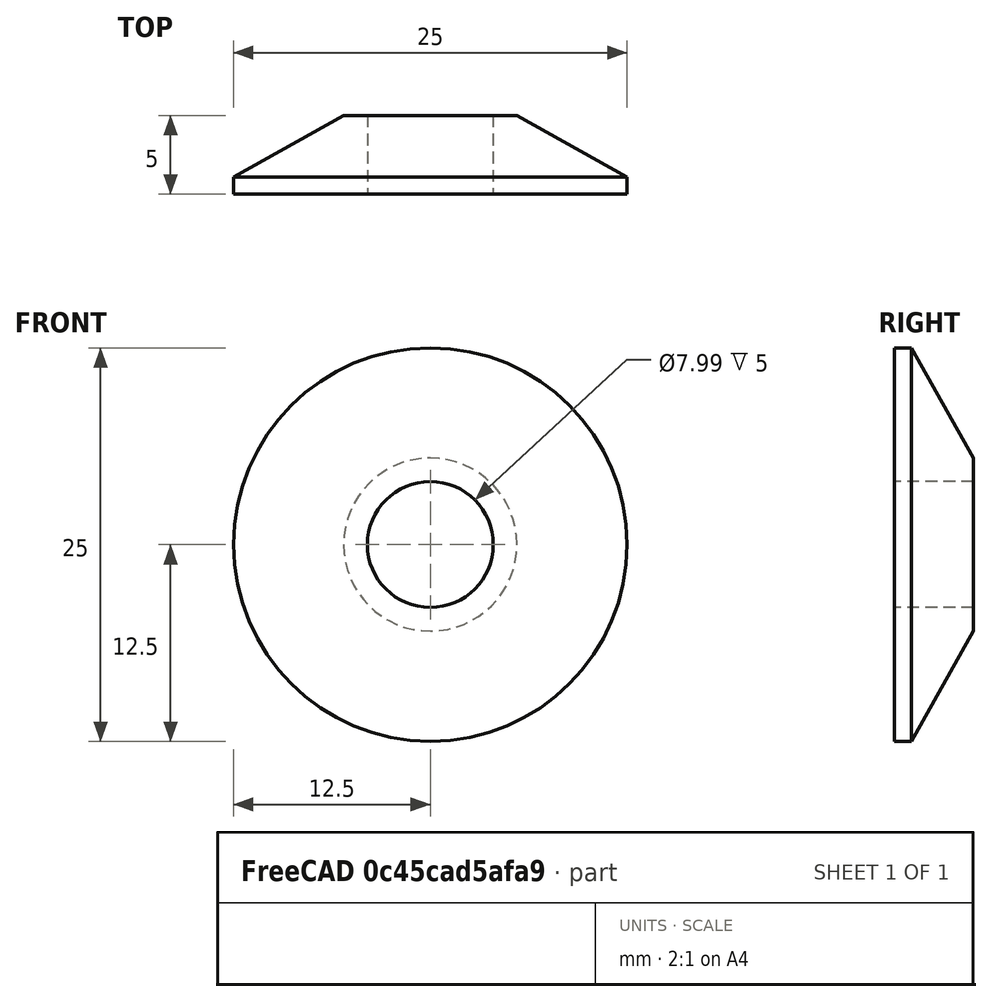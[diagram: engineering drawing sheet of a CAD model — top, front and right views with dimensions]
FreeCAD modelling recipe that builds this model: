
FCSTD DOCUMENT  (FreeCAD 1.0R39109 (Git))
Label: Прижим лезвия
License: All rights reserved
LicenseURL: https://en.wikipedia.org/wiki/All_rights_reserved
objects: Sketcher::SketchObject×1, PartDesign::Revolution×1, PartDesign::Body×1
note: 6 computed .brp shape members not serialized (recipe doc carries the construction recipe); baked Part::Feature solids carry a one-line shape summary decoded from their .brp

FEATURE [Sketcher::SketchObject] Sketch
  ArcFitTolerance = 1e-06
  AttachmentSupport = -> [XY_Plane]
  FullyConstrained = false
  MakeInternals = false
  MapMode = 5
  sketch-geometry (5):
    g0: LineSegment StartX=3.99715 StartY=0 StartZ=0 EndX=12.4972 EndY=0 EndZ=0
    g1: LineSegment StartX=12.4972 StartY=0 StartZ=0 EndX=12.4972 EndY=1.07894 EndZ=0
    g2: LineSegment StartX=5.49826 StartY=5 StartZ=0 EndX=3.99715 EndY=5 EndZ=0
    g3: LineSegment StartX=3.99715 StartY=5 StartZ=0 EndX=3.99715 EndY=0 EndZ=0
    g4: LineSegment StartX=5.49826 StartY=5 StartZ=0 EndX=12.4972 EndY=1.07894 EndZ=0
  constraints (12):
    c: Coincident(g0,g1)
    c: Coincident(g2,g3)
    c: Coincident(g3,g0)
    c: Horizontal(g0)
    c: Horizontal(g2)
    c: Vertical(g1)
    c: Vertical(g3)
    c: Distance(g1,g3) = 8.5
    c: Distance(g0,g2) = 5
    c: PointOnObject(g0,g-1)
    c: Coincident(g2,g4)
    c: Coincident(g1,g4)
FEATURE [PartDesign::Revolution] Revolution
  Angle = 360
  Angle2 = 60
  Axis = (0,1,0)
  Base = (0,0,0)
  Profile = -> Sketch
  ReferenceAxis = -> Sketch [V_Axis]
  Refine = true
  Reversed = true
  Suppressed = false
  Type = 0
FEATURE [PartDesign::Body] Body  label="Тело"
  AllowCompound = false
  Group = -> [Sketch,Revolution]
  Origin = -> Origin
  Tip = -> Revolution
